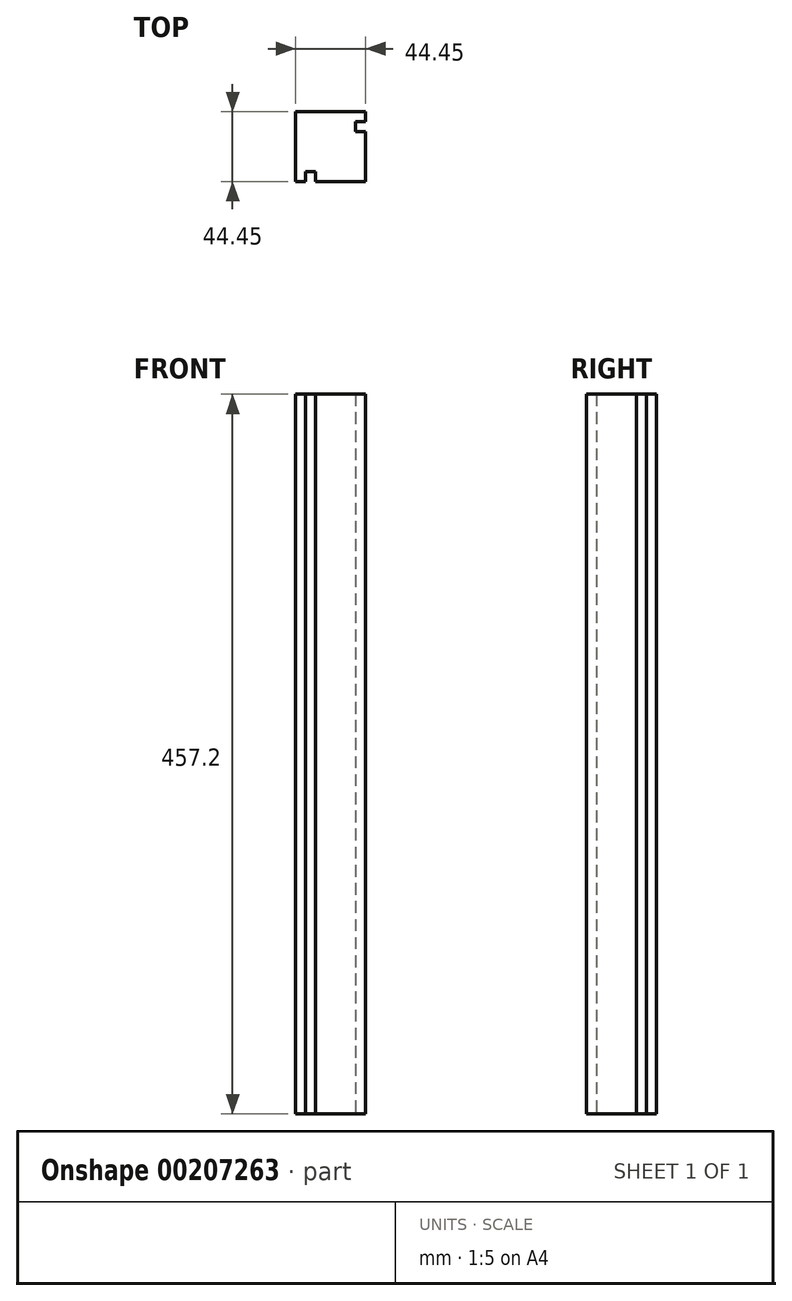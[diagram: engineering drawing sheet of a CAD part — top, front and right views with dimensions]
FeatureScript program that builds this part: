
annotation { "Feature Type Name" : "Feature", "Feature Type Description" : "" }
export const myFeature = defineFeature(function(context is Context, id is Id, definition is map)
    precondition{}
    {
        {
            var Q0;
            Q0=qCreatedBy(makeId("Top.planeOp"),FACE);
            var sketch = newSketch(context, id + "F0", { "sketchPlane" : qUnion([Q0])});
            skLineSegment(sketch, "E0", {"start": v(0, 0) * mm, "end": v(0, 44.45) * mm});
            skLineSegment(sketch, "E1", {"start": v(0, 44.45) * mm, "end": v(44.45, 44.45) * mm});
            skLineSegment(sketch, "E2", {"start": v(44.45, 44.45) * mm, "end": v(44.45, 38.1) * mm});
            skLineSegment(sketch, "E3", {"start": v(44.45, 38.1) * mm, "end": v(38.1, 38.1) * mm});
            skLineSegment(sketch, "E4", {"start": v(38.1, 38.1) * mm, "end": v(38.1, 31.75) * mm});
            skLineSegment(sketch, "E5", {"start": v(38.1, 31.75) * mm, "end": v(44.45, 31.75) * mm});
            skLineSegment(sketch, "E6", {"start": v(44.45, 31.75) * mm, "end": v(44.45, 0) * mm});
            skLineSegment(sketch, "E7", {"start": v(44.45, 0) * mm, "end": v(12.7, 0) * mm});
            skLineSegment(sketch, "E8", {"start": v(12.7, 0) * mm, "end": v(12.7, 6.35) * mm});
            skLineSegment(sketch, "E9", {"start": v(12.7, 6.35) * mm, "end": v(6.35, 6.35) * mm});
            skLineSegment(sketch, "E10", {"start": v(6.35, 6.35) * mm, "end": v(6.35, 0) * mm});
            skLineSegment(sketch, "E11", {"start": v(6.35, 0) * mm, "end": v(0, 0) * mm});
            skSolve(sketch);
        }
        {
            var Q0;
            Q0=makeQuery(id+"F0.imprint","IMPRINT",FACE,{"disambiguationData":[TD([[makeQuery(id+"F0.imprint","IMPRINT",EDGE,{"derivedFrom":sQuery(id+"F0.wireOp",EDGE,"E0")}),-1.0]])]});
            extrude(context, id + "F1", {"entities" : qUnion([Q0]), "depth" : 457.2 * mm});
        }
    });
